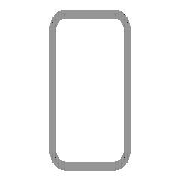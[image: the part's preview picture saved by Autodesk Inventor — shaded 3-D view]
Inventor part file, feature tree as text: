
AUTODESK INVENTOR PART (.ipt)
format: ipt  version: 2025 (Build 290162010, 162A)  size: 153,600 bytes
history: native  units: mm (DEFAULTED — no unit token found)
features: other x3, sketch x2, extrude x1, plane x1
ambient origin geometry x8: Origin, YZ Plane, XZ Plane, XY Plane, X Axis, Y Axis, Z Axis, Center Point
bodies: Solid1 (feature_tree), Body (feature_tree)
feature tree (7):
  other  "Driven Length"
  other  "Start plane"
  other  "End plane"
  extrude  "Extrusion2"  TaperAngle=0.0deg  [1 undecoded]
  sketch  "Sketch3"  dims[d3=4381.295mm d4=0.0mm]
  plane  "Work Plane3"
  sketch  "Sketch5"  dims[d7=4.0mm d9=40.0mm d11=80.0mm d12=2.0mm d13=-0.0mm d14=4381.295mm d15=20.0mm d16=40.0mm d17=90.0deg d18=4381.295mm d19=9.86111mm d20=5.846853mm d21=0.0mm d22=0.0mm]
note: 1 required parameter value undecoded (feature->parameter linkage not recoverable at this tier; creation-order binding heuristic only, values carry confidence <= 0.55)
